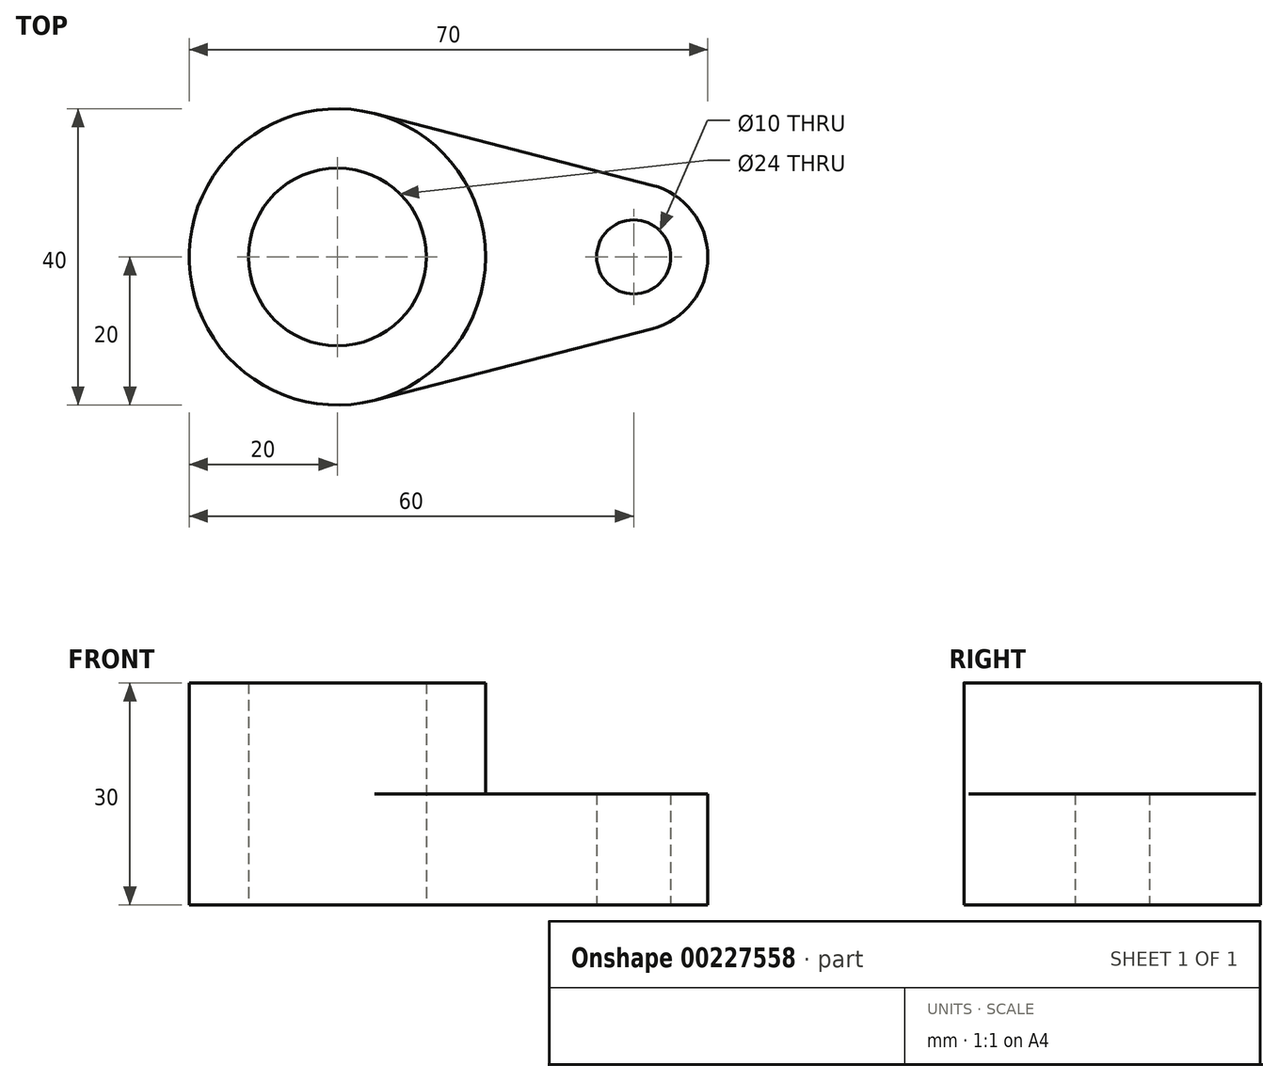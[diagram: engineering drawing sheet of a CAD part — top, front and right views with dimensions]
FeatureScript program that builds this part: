
annotation { "Feature Type Name" : "Feature", "Feature Type Description" : "" }
export const myFeature = defineFeature(function(context is Context, id is Id, definition is map)
    precondition{}
    {
        {
            var Q0;
            Q0=qCreatedBy(makeId("Top.planeOp"),FACE);
            var sketch = newSketch(context, id + "F0", { "sketchPlane" : qUnion([Q0])});
            skCircle(sketch, "E0", {"center": v(0, 0) * mm, "radius": 12 * mm});
            skCircle(sketch, "E1", {"center": v(40, 0) * mm, "radius": 5 * mm});
            skArc(sketch, "E2", {"start": v(42.5, -9.68) * mm, "mid": v(50, 0) * mm, "end": v(42.5, 9.68) * mm});
            skCircle(sketch, "E3", {"center": v(0, 0) * mm, "radius": 20 * mm});
            skLineSegment(sketch, "E4", {"start": v(5, 19.36) * mm, "end": v(42.5, 9.68) * mm});
            skLineSegment(sketch, "E5", {"start": v(5, -19.36) * mm, "end": v(42.5, -9.68) * mm});
            skSolve(sketch);
        }
        {
            var Q0;
            Q0=makeQuery(id+"F0.imprint","IMPRINT",FACE,{"disambiguationData":[TD([[makeQuery(id+"F0.imprint","IMPRINT",EDGE,{"derivedFrom":sQuery(id+"F0.wireOp",EDGE,"E1")}),-1.0]])]});
            extrude(context, id + "F1", {"entities" : qUnion([Q0]), "depth" : 15 * mm});
        }
        {
            var Q0;
            Q0=makeQuery(id+"F0.imprint","IMPRINT",FACE,{"disambiguationData":[TD([[makeQuery(id+"F0.imprint","IMPRINT",EDGE,{"derivedFrom":sQuery(id+"F0.wireOp",EDGE,"E0")}),-1.0]])]});
            extrude(context, id + "F2", {"entities" : qUnion([Q0]), "operationType" : NewBodyOperationType.ADD, "depth" : 30 * mm});
        }
    });
